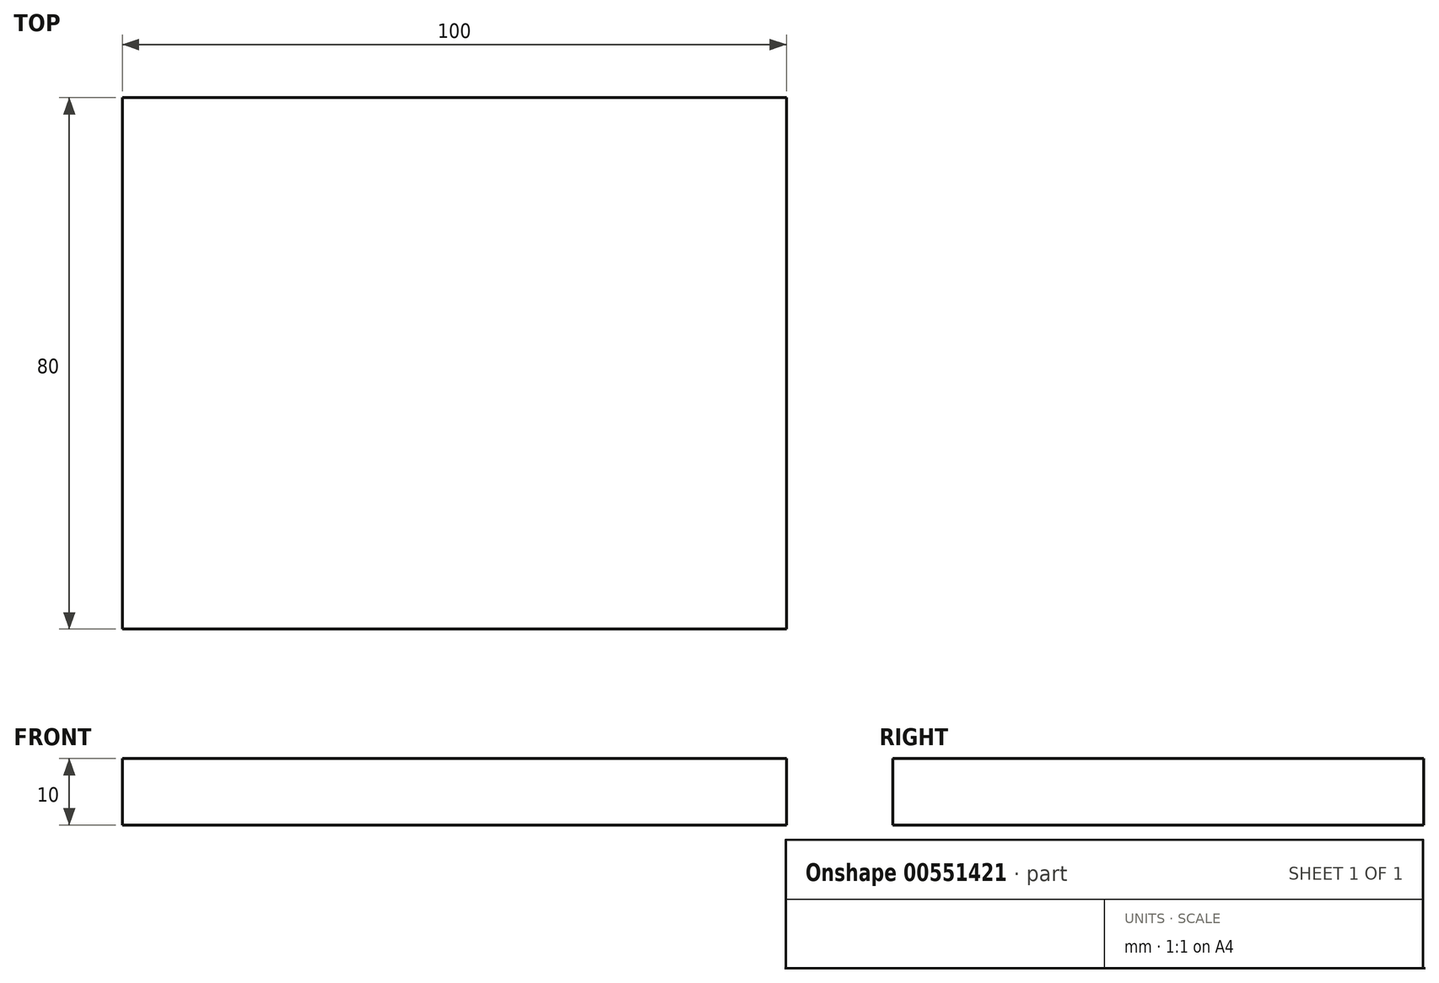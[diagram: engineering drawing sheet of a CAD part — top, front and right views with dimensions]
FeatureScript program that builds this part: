
annotation { "Feature Type Name" : "Feature", "Feature Type Description" : "" }
export const myFeature = defineFeature(function(context is Context, id is Id, definition is map)
    precondition{}
    {
        {
            var Q0;
            Q0=qCreatedBy(makeId("Top.planeOp"),FACE);
            var sketch = newSketch(context, id + "F0", { "sketchPlane" : qUnion([Q0])});
            skLineSegment(sketch, "E0.bottom", {"start": v(50, 40) * mm, "end": v(-50, 40) * mm});
            skLineSegment(sketch, "E0.top", {"start": v(50, -40) * mm, "end": v(-50, -40) * mm});
            skLineSegment(sketch, "E0.left", {"start": v(50, 40) * mm, "end": v(50, -40) * mm});
            skLineSegment(sketch, "E0.right", {"start": v(-50, 40) * mm, "end": v(-50, -40) * mm});
            skPoint(sketch, "E0.middle", {"position": v(0, 0) * mm});
            skSolve(sketch);
        }
        {
            var Q0;
            Q0=makeQuery(id+"F0.imprint","IMPRINT",FACE,{"disambiguationData":[TD([[makeQuery(id+"F0.imprint","IMPRINT",EDGE,{"derivedFrom":sQuery(id+"F0.wireOp",EDGE,"E0.bottom")}),1.0]])]});
            extrude(context, id + "F1", {"entities" : qUnion([Q0]), "depth" : 10 * mm, "offsetDistance" : 25.4 * mm});
        }
    });
